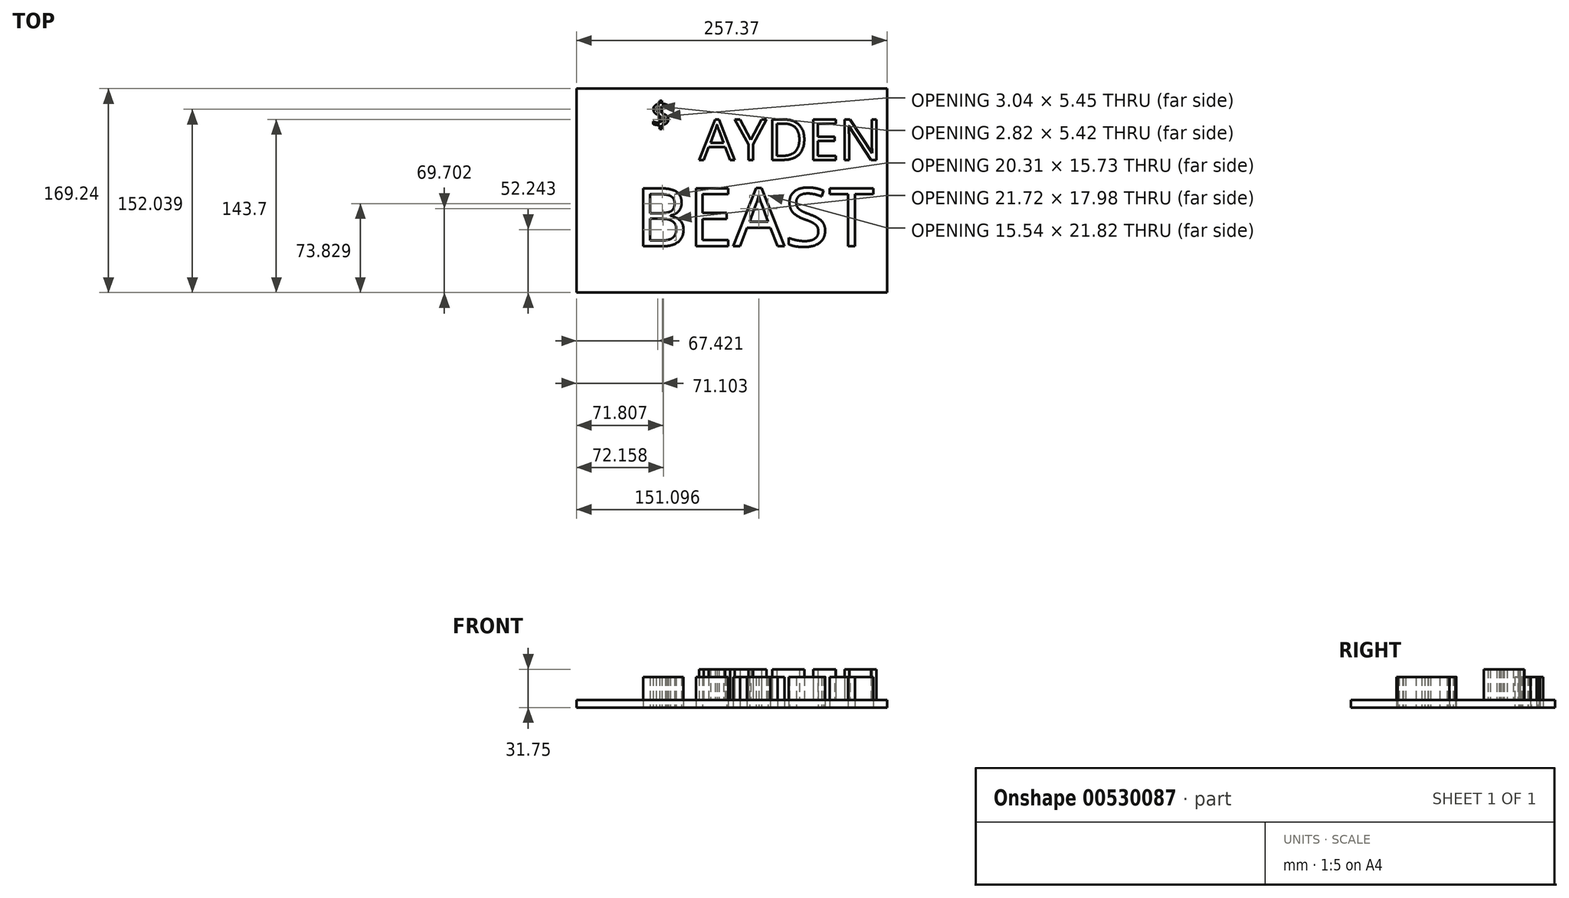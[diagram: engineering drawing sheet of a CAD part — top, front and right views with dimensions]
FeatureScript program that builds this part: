
annotation { "Feature Type Name" : "Feature", "Feature Type Description" : "" }
export const myFeature = defineFeature(function(context is Context, id is Id, definition is map)
    precondition{}
    {
        {
            var Q0;
            Q0=qCreatedBy(makeId("Top.planeOp"),FACE);
            var sketch = newSketch(context, id + "F0", { "sketchPlane" : qUnion([Q0])});
            skText(sketch, "E0", { "text": "BEAST", "fontName": "OpenSans-Regular.ttf"});
            const initialGuessF0  = {"E0": [-0.05596, -0.04845, 1, 0, 0.04845]};
            skSetInitialGuess(sketch, initialGuessF0);
            skSolve(sketch);
        }
        {
            var Q0;
            Q0 = qSketchRegion(id + "F0", true);
            extrude(context, id + "F1", {"entities" : qUnion([Q0]), "depth" : 25.4 * mm, "offsetDistance" : 25.4 * mm});
        }
        {
            var Q0;
            Q0=qCreatedBy(makeId("Top.planeOp"),FACE);
            var sketch = newSketch(context, id + "F2", { "sketchPlane" : qUnion([Q0])});
            skText(sketch, "E1", { "text": "$", "fontName": "OpenSans-Regular.ttf"});
            const initialGuessF2  = {"E1": [-0.04318, 0.0505, 1, 0, 0.02067]};
            skSetInitialGuess(sketch, initialGuessF2);
            skSolve(sketch);
        }
        {
            var Q0;
            Q0 = qSketchRegion(id + "F2", true);
            extrude(context, id + "F3", {"entities" : qUnion([Q0]), "depth" : 25.4 * mm, "offsetDistance" : 25.4 * mm});
        }
        {
            var Q0;
            Q0=qCreatedBy(makeId("Top.planeOp"),FACE);
            var sketch = newSketch(context, id + "F4", { "sketchPlane" : qUnion([Q0])});
            skLineSegment(sketch, "E2.bottom", {"start": v(-104.72, 82.3) * mm, "end": v(152.65, 82.3) * mm});
            skLineSegment(sketch, "E2.top", {"start": v(-104.72, -86.94) * mm, "end": v(152.65, -86.94) * mm});
            skLineSegment(sketch, "E2.left", {"start": v(-104.72, 82.3) * mm, "end": v(-104.72, -86.94) * mm});
            skLineSegment(sketch, "E2.right", {"start": v(152.65, 82.3) * mm, "end": v(152.65, -86.94) * mm});
            skSolve(sketch);
        }
        {
            var Q0;
            Q0=makeQuery(id+"F4.imprint","IMPRINT",FACE,{"disambiguationData":[TD([[makeQuery(id+"F4.imprint","IMPRINT",EDGE,{"derivedFrom":sQuery(id+"F4.wireOp",EDGE,"E2.bottom")}),-1.0]])]});
            extrude(context, id + "F5", {"entities" : qUnion([Q0]), "depth" : 6.35 * mm, "offsetDistance" : 25.4 * mm});
        }
        {
            var Q0;
            Q0=makeQuery(id+"F5.opExtrude","CAP_FACE",FACE,{"disambiguationData":[OSD([sQuery(id+"F4.wireOp",EDGE,"E2.bottom"),sQuery(id+"F4.wireOp",EDGE,"E2.top"),sQuery(id+"F4.wireOp",EDGE,"E2.left"),sQuery(id+"F4.wireOp",EDGE,"E2.right")])],"isStart":false});
            var sketch = newSketch(context, id + "F6", { "sketchPlane" : qUnion([Q0])});
            skText(sketch, "E3", { "text": "AYDEN", "fontName": "OpenSans-Regular.ttf"});
            const initialGuessF6  = {"E3": [-0.00312, 0.02316, 1, 0, 0.03374]};
            skSetInitialGuess(sketch, initialGuessF6);
            skSolve(sketch);
        }
        {
            var Q0;
            Q0 = qSketchRegion(id + "F6", true);
            extrude(context, id + "F7", {"entities" : qUnion([Q0]), "operationType" : NewBodyOperationType.ADD, "depth" : 25.4 * mm, "offsetDistance" : 25.4 * mm});
        }
    });
